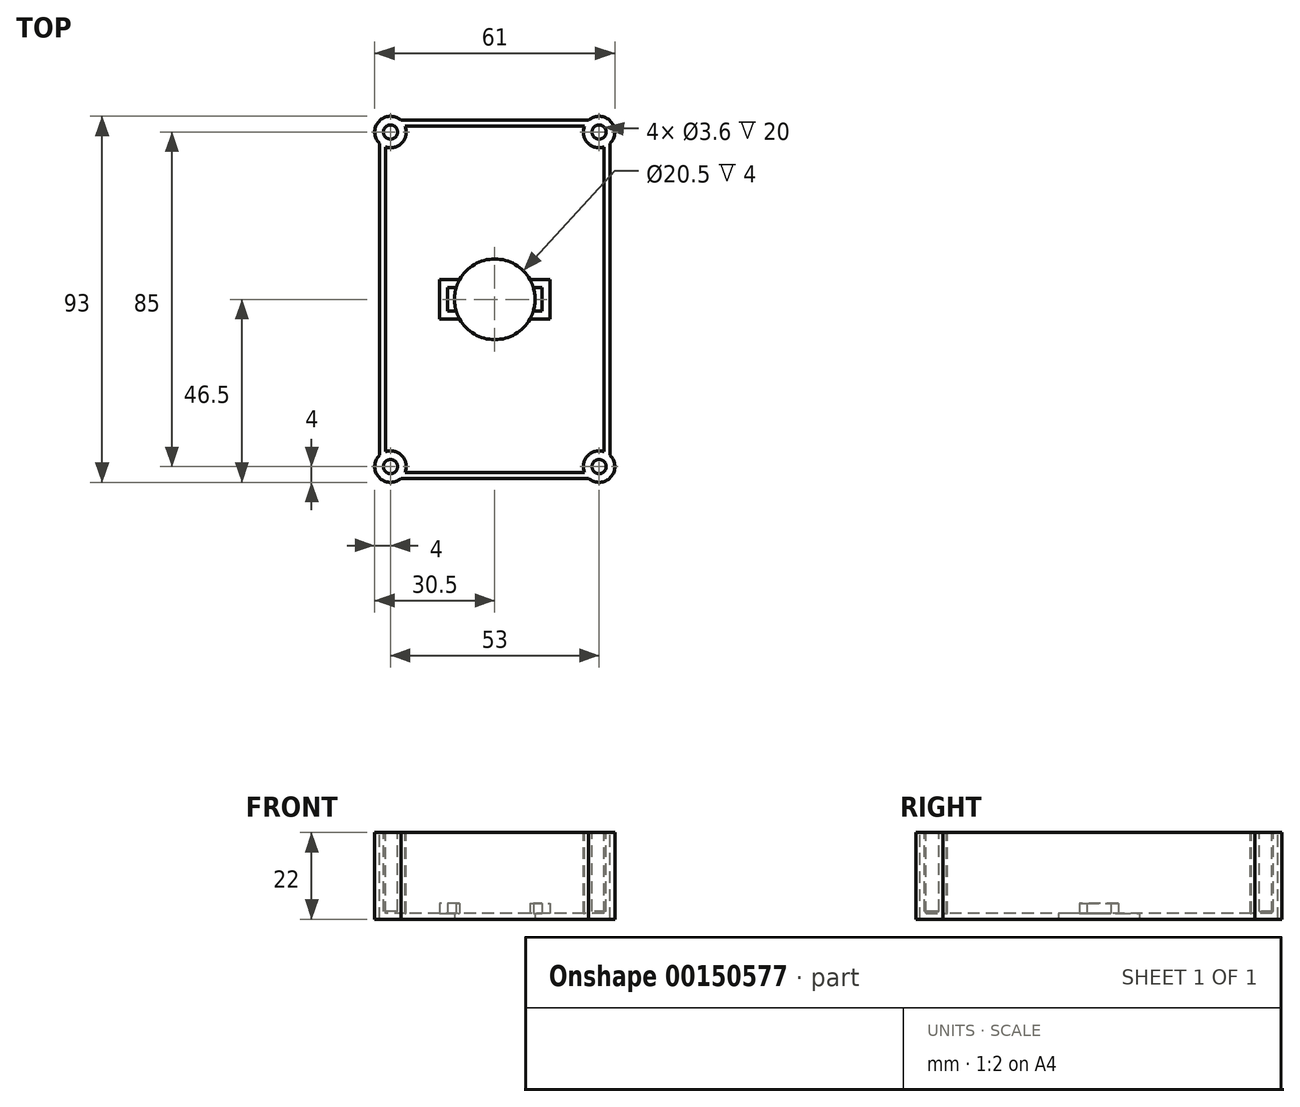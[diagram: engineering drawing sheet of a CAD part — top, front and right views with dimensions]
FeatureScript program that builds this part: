
annotation { "Feature Type Name" : "Feature", "Feature Type Description" : "" }
export const myFeature = defineFeature(function(context is Context, id is Id, definition is map)
    precondition{}
    {
        {
            var Q0;
            Q0=qCreatedBy(makeId("Top.planeOp"),FACE);
            var sketch = newSketch(context, id + "F0", { "sketchPlane" : qUnion([Q0])});
            skLineSegment(sketch, "E0.bottom", {"start": v(29.25, 45.5) * mm, "end": v(-29.25, 45.5) * mm});
            skLineSegment(sketch, "E0.top", {"start": v(29.25, -45.5) * mm, "end": v(-29.25, -45.5) * mm});
            skLineSegment(sketch, "E0.left", {"start": v(29.25, 45.5) * mm, "end": v(29.25, -45.5) * mm});
            skLineSegment(sketch, "E0.right", {"start": v(-29.25, 45.5) * mm, "end": v(-29.25, -45.5) * mm});
            skPoint(sketch, "E0.middle", {"position": v(0, 0) * mm});
            skSolve(sketch);
        }
        {
            var Q0;
            Q0=qSketchRegion(id+"F0",true);
            extrude(context, id + "F1", {"entities" : qUnion([Q0]), "oppositeDirection" : true, "depth" : 22 * mm});
        }
        {
            var Q0;
            Q0=makeQuery(id+"F1.opExtrude","CAP_FACE",FACE,{"disambiguationData":[OSD([sQuery(id+"F0.wireOp",EDGE,"E0.bottom"),sQuery(id+"F0.wireOp",EDGE,"E0.top"),sQuery(id+"F0.wireOp",EDGE,"E0.left"),sQuery(id+"F0.wireOp",EDGE,"E0.right")])],"isStart":true});
            shell(context, id + "F2", {"entities" : qUnion([Q0]), "thickness" : 1.5 * mm});
        }
        {
            var Q0;
            Q0=makeQuery(id+"F1.opExtrude","SWEPT_EDGE",EDGE,{"disambiguationData":[OSD([sQuery(id+"F0.wireOp",EDGE,"E0.bottom"),sQuery(id+"F0.wireOp",EDGE,"E0.right")])]});
            var Q1;
            Q1=makeQuery(id+"F1.opExtrude","SWEPT_EDGE",EDGE,{"disambiguationData":[OSD([sQuery(id+"F0.wireOp",EDGE,"E0.bottom"),sQuery(id+"F0.wireOp",EDGE,"E0.left")])]});
            var Q2;
            Q2=makeQuery(id+"F1.opExtrude","SWEPT_EDGE",EDGE,{"disambiguationData":[OSD([sQuery(id+"F0.wireOp",EDGE,"E0.top"),sQuery(id+"F0.wireOp",EDGE,"E0.right")])]});
            var Q3;
            Q3=makeQuery(id+"F1.opExtrude","SWEPT_EDGE",EDGE,{"disambiguationData":[OSD([sQuery(id+"F0.wireOp",EDGE,"E0.top"),sQuery(id+"F0.wireOp",EDGE,"E0.left")])]});
            fillet(context, id + "F3", {"entities" : qUnion([Q0, Q1, Q2, Q3]), "radius" : 3 * mm, "tangentPropagation" : true, "allowEdgeOverflow" : false});
        }
        {
            var Q0;
            Q0=makeQuery(id+"F2.opShell","OFFSET_EDGE",EDGE,{"disambiguationData":[OSD([sQuery(id+"F0.wireOp",EDGE,"E0.bottom"),sQuery(id+"F0.wireOp",EDGE,"E0.right")])]});
            var Q1;
            Q1=makeQuery(id+"F2.opShell","OFFSET_EDGE",EDGE,{"disambiguationData":[OSD([sQuery(id+"F0.wireOp",EDGE,"E0.top"),sQuery(id+"F0.wireOp",EDGE,"E0.right")])]});
            var Q2;
            Q2=makeQuery(id+"F2.opShell","OFFSET_EDGE",EDGE,{"disambiguationData":[OSD([sQuery(id+"F0.wireOp",EDGE,"E0.top"),sQuery(id+"F0.wireOp",EDGE,"E0.left")])]});
            var Q3;
            Q3=makeQuery(id+"F2.opShell","OFFSET_EDGE",EDGE,{"disambiguationData":[OSD([sQuery(id+"F0.wireOp",EDGE,"E0.bottom"),sQuery(id+"F0.wireOp",EDGE,"E0.left")])]});
            fillet(context, id + "F4", {"entities" : qUnion([Q0, Q1, Q2, Q3]), "radius" : 2 * mm, "tangentPropagation" : true, "allowEdgeOverflow" : false});
        }
        {
            var Q0;
            Q0=makeQuery(id+"F0.imprint","IMPRINT",FACE,{"disambiguationData":[TD([[makeQuery(id+"F0.imprint","IMPRINT",EDGE,{"derivedFrom":sQuery(id+"F0.wireOp",EDGE,"E0.bottom")}),1.0]])]});
            var sketch = newSketch(context, id + "F5", { "sketchPlane" : qUnion([Q0])});
            skLineSegment(sketch, "E1", {"start": v(26.5, -42.5) * mm, "end": v(26.5, 42.5) * mm, "construction": true});
            skLineSegment(sketch, "E2", {"start": v(-26.5, 42.5) * mm, "end": v(-26.5, -42.5) * mm, "construction": true});
            skLineSegment(sketch, "E3", {"start": v(26.5, -42.5) * mm, "end": v(-26.5, -42.5) * mm, "construction": true});
            skLineSegment(sketch, "E4", {"start": v(26.5, 42.5) * mm, "end": v(-26.5, 42.5) * mm, "construction": true});
            skCircle(sketch, "E5", {"center": v(26.5, -42.5) * mm, "radius": 4 * mm});
            skCircle(sketch, "E6", {"center": v(26.5, 42.5) * mm, "radius": 4 * mm});
            skCircle(sketch, "E7", {"center": v(-26.5, 42.5) * mm, "radius": 4 * mm});
            skCircle(sketch, "E8", {"center": v(-26.5, -42.5) * mm, "radius": 4 * mm});
            skSolve(sketch);
        }
        {
            var Q0;
            Q0=qSketchRegion(id+"F5",true);
            extrude(context, id + "F6", {"entities" : qUnion([Q0]), "operationType" : NewBodyOperationType.ADD, "oppositeDirection" : true, "depth" : 22 * mm});
        }
        {
            var Q0;
            Q0=qCreatedBy(makeId("Top.planeOp"),FACE);
            var sketch = newSketch(context, id + "F7", { "sketchPlane" : qUnion([Q0])});
            skCircle(sketch, "E9", {"center": v(26.5, -42.5) * mm, "radius": 1.8 * mm});
            skCircle(sketch, "E10", {"center": v(26.5, 42.5) * mm, "radius": 1.8 * mm});
            skCircle(sketch, "E11", {"center": v(-26.5, -42.5) * mm, "radius": 1.8 * mm});
            skCircle(sketch, "E12", {"center": v(-26.5, 42.5) * mm, "radius": 1.8 * mm});
            skSolve(sketch);
        }
        {
            var Q0;
            Q0=qSketchRegion(id+"F7",true);
            extrude(context, id + "F8", {"entities" : qUnion([Q0]), "operationType" : NewBodyOperationType.REMOVE, "oppositeDirection" : true, "depth" : 20 * mm});
        }
        {
            var Q0;
            Q0=makeQuery(id+"F0.imprint","IMPRINT",FACE,{"disambiguationData":[TD([[makeQuery(id+"F0.imprint","IMPRINT",EDGE,{"derivedFrom":sQuery(id+"F0.wireOp",EDGE,"E0.bottom")}),1.0]])]});
            var sketch = newSketch(context, id + "F9", { "sketchPlane" : qUnion([Q0])});
            skArc(sketch, "E13", {"start": v(27.75, -37.9) * mm, "mid": v(21.78, -38.03) * mm, "end": v(21.9, -44) * mm, "construction": true});
            skArc(sketch, "E14", {"start": v(21.9, 44) * mm, "mid": v(21.78, 38.03) * mm, "end": v(27.75, 37.9) * mm, "construction": true});
            skArc(sketch, "E15", {"start": v(-25.85, 35.82) * mm, "mid": v(-19.79, 37.94) * mm, "end": v(-21.9, 44) * mm, "construction": true});
            skArc(sketch, "E16", {"start": v(-21.9, -44) * mm, "mid": v(-22.32, -40.44) * mm, "end": v(-25.85, -39.82) * mm, "construction": true});
            skLineSegment(sketch, "E17", {"start": v(-25.85, -39.82) * mm, "end": v(-25.85, 35.82) * mm, "construction": true});
            skLineSegment(sketch, "E18", {"start": v(-21.9, 44) * mm, "end": v(21.9, 44) * mm, "construction": true});
            skLineSegment(sketch, "E19", {"start": v(27.75, -37.9) * mm, "end": v(27.75, 37.9) * mm, "construction": true});
            skLineSegment(sketch, "E20", {"start": v(21.9, -44) * mm, "end": v(-21.9, -44) * mm, "construction": true});
            skSolve(sketch);
        }
        {
            var Q0;
            Q0=makeQuery(id+"F6.boolean.opBoolean","MERGE",FACE,{"derivedFrom":[makeQuery(id+"F1.opExtrude","CAP_FACE",FACE,{"disambiguationData":[OSD([sQuery(id+"F0.wireOp",EDGE,"E0.bottom"),sQuery(id+"F0.wireOp",EDGE,"E0.top"),sQuery(id+"F0.wireOp",EDGE,"E0.left"),sQuery(id+"F0.wireOp",EDGE,"E0.right")])],"isStart":false}),makeQuery(id+"F6.opExtrude","CAP_FACE",FACE,{"disambiguationData":[OSD([sQuery(id+"F5.wireOp",EDGE,"E5")])],"isStart":false}),makeQuery(id+"F6.opExtrude","CAP_FACE",FACE,{"disambiguationData":[OSD([sQuery(id+"F5.wireOp",EDGE,"E6")])],"isStart":false}),makeQuery(id+"F6.opExtrude","CAP_FACE",FACE,{"disambiguationData":[OSD([sQuery(id+"F5.wireOp",EDGE,"E7")])],"isStart":false}),makeQuery(id+"F6.opExtrude","CAP_FACE",FACE,{"disambiguationData":[OSD([sQuery(id+"F5.wireOp",EDGE,"E8")])],"isStart":false})]});
            var sketch = newSketch(context, id + "F10", { "sketchPlane" : qUnion([Q0])});
            skCircle(sketch, "E21", {"center": v(0, 0) * mm, "radius": 10.25 * mm});
            skSolve(sketch);
        }
        {
            var Q0;
            Q0=makeQuery(id+"F1.opExtrude","CAP_FACE",FACE,{"disambiguationData":[OSD([sQuery(id+"F0.wireOp",EDGE,"E0.bottom"),sQuery(id+"F0.wireOp",EDGE,"E0.top"),sQuery(id+"F0.wireOp",EDGE,"E0.left"),sQuery(id+"F0.wireOp",EDGE,"E0.right")])],"isStart":false});
            var sketch = newSketch(context, id + "F11", { "sketchPlane" : qUnion([Q0])});
            skLineSegment(sketch, "E22", {"start": v(14, -5) * mm, "end": v(-14, -5) * mm});
            skLineSegment(sketch, "E23", {"start": v(-14, -5) * mm, "end": v(-14, 5) * mm});
            skLineSegment(sketch, "E24", {"start": v(-14, 5) * mm, "end": v(14, 5) * mm});
            skLineSegment(sketch, "E25", {"start": v(14, -5) * mm, "end": v(14, 5) * mm});
            skLineSegment(sketch, "E26", {"start": v(12, -3) * mm, "end": v(12, 3) * mm});
            skLineSegment(sketch, "E27", {"start": v(12, 3) * mm, "end": v(-12, 3) * mm});
            skLineSegment(sketch, "E28", {"start": v(12, -3) * mm, "end": v(-12, -3) * mm});
            skLineSegment(sketch, "E29", {"start": v(-12, 3) * mm, "end": v(-12, -3) * mm});
            skSolve(sketch);
        }
        {
            var Q0;
            Q0 = qSketchRegion(id + "F11", true);
            extrude(context, id + "F12", {"entities" : qUnion([Q0]), "operationType" : NewBodyOperationType.ADD, "oppositeDirection" : true, "depth" : 4 * mm});
        }
        {
            var Q0;
            Q0 = qSketchRegion(id + "F10", true);
            extrude(context, id + "F13", {"entities" : qUnion([Q0]), "operationType" : NewBodyOperationType.REMOVE, "oppositeDirection" : true, "depth" : 25 * mm});
        }
    });
